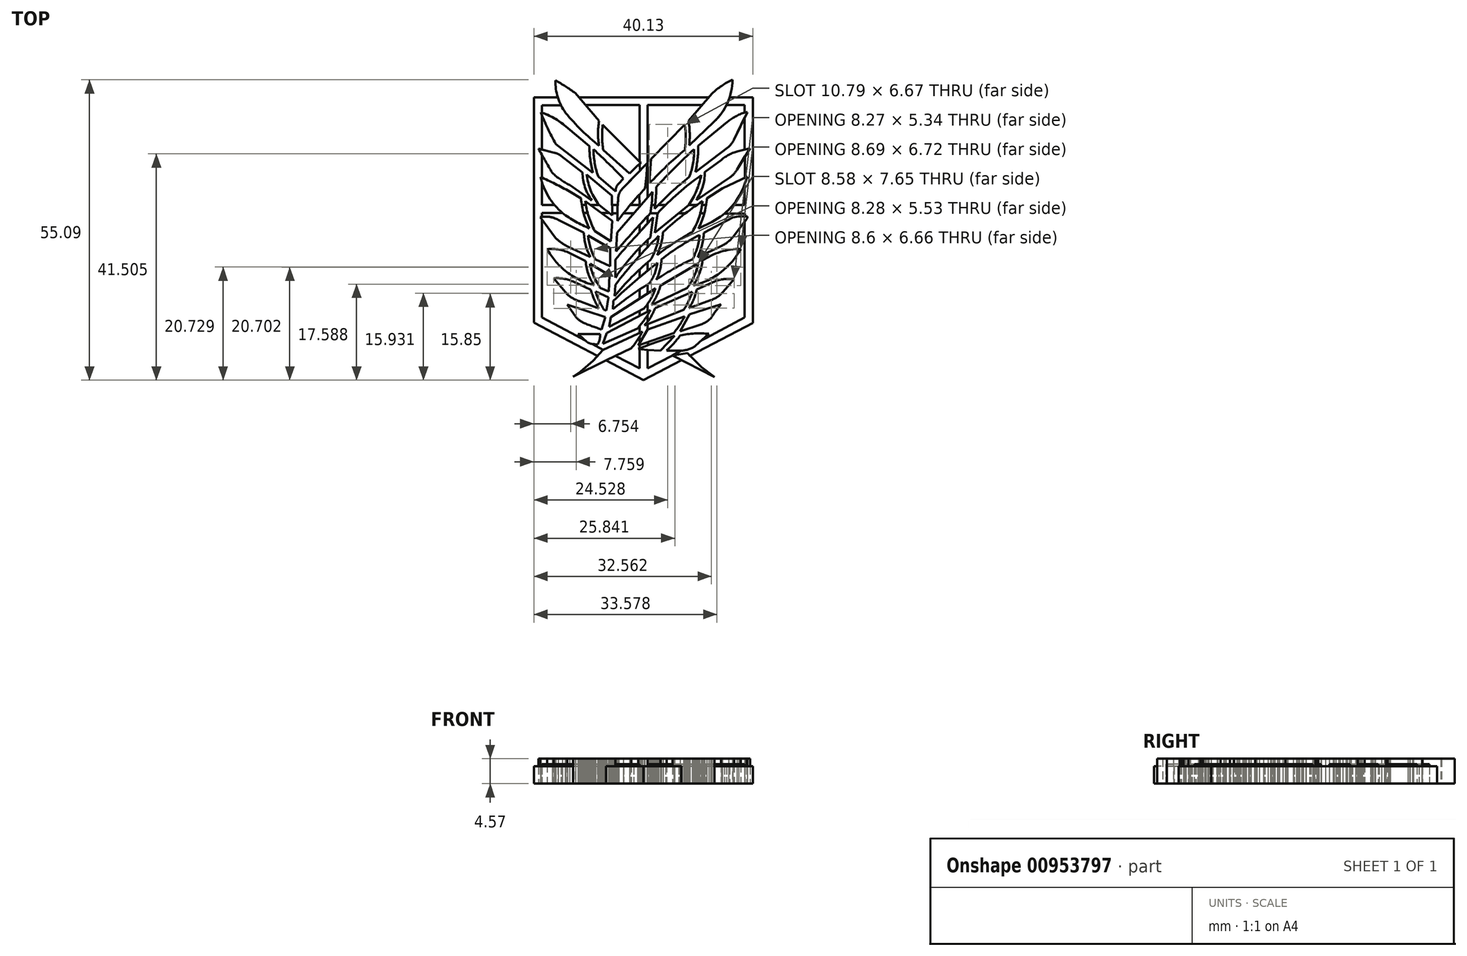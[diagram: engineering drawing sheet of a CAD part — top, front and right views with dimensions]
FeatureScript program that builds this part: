
annotation { "Feature Type Name" : "Feature", "Feature Type Description" : "" }
export const myFeature = defineFeature(function(context is Context, id is Id, definition is map)
    precondition{}
    {
        {
            var Q0;
            Q0=qCreatedBy(makeId("Top.planeOp"),FACE);
            var sketch = newSketch(context, id + "F0", { "sketchPlane" : qUnion([Q0])});
            skLineSegment(sketch, "E0", {"start": v(16.1, 29.15) * mm, "end": v(20.24, 29.15) * mm});
            skLineSegment(sketch, "E1", {"start": v(12.17, 29.15) * mm, "end": v(0, 29.15) * mm});
            skLineSegment(sketch, "E2", {"start": v(0, 29.15) * mm, "end": v(-11.4, 29.15) * mm});
            skLineSegment(sketch, "E3", {"start": v(-15.52, 29.15) * mm, "end": v(-19.9, 29.15) * mm});
            skLineSegment(sketch, "E4", {"start": v(-19.9, 29.15) * mm, "end": v(-19.9, 11.09) * mm});
            skLineSegment(sketch, "E5", {"start": v(-19.9, 11.09) * mm, "end": v(-19.9, -12.23) * mm});
            skLineSegment(sketch, "E6", {"start": v(20.24, 29.15) * mm, "end": v(20.24, -12.05) * mm});
            skLineSegment(sketch, "E7", {"start": v(20.24, -12.05) * mm, "end": v(20.24, -12.29) * mm});
            skLineSegment(sketch, "E8", {"start": v(20.24, -12.29) * mm, "end": v(8.8, -18.24) * mm});
            skLineSegment(sketch, "E9", {"start": v(-19.9, -12.23) * mm, "end": v(-8.29, -18.3) * mm});
            skLineSegment(sketch, "E10", {"start": v(7.13, -19.12) * mm, "end": v(0.17, -22.74) * mm});
            skLineSegment(sketch, "E11", {"start": v(-6.69, -19.14) * mm, "end": v(0.17, -22.74) * mm});
            skLineSegment(sketch, "E12", {"start": v(13.24, -22.16) * mm, "end": v(5.55, -18.25) * mm});
            skLineSegment(sketch, "E13", {"start": v(5.55, -18.25) * mm, "end": v(8.26, -17.77) * mm});
            skLineSegment(sketch, "E14", {"start": v(5.55, -18.25) * mm, "end": v(7.07, -17.34) * mm});
            skLineSegment(sketch, "E15", {"start": v(7.07, -17.34) * mm, "end": v(4.43, -17.34) * mm});
            skLineSegment(sketch, "E16", {"start": v(5.55, -18.25) * mm, "end": v(0.97, -20.6) * mm});
            skLineSegment(sketch, "E17", {"start": v(0.97, -20.6) * mm, "end": v(0.97, -17.2) * mm});
            skLineSegment(sketch, "E18", {"start": v(0.97, -17.2) * mm, "end": v(3.32, -17.33) * mm});
            skLineSegment(sketch, "E19", {"start": v(3.32, -17.33) * mm, "end": v(5.93, -14.63) * mm});
            skLineSegment(sketch, "E20", {"start": v(5.93, -14.63) * mm, "end": v(1.54, -16.12) * mm});
            skLineSegment(sketch, "E21", {"start": v(1.54, -16.12) * mm, "end": v(-0.76, -17.04) * mm});
            skLineSegment(sketch, "E22", {"start": v(-0.76, -17.04) * mm, "end": v(0.97, -17.2) * mm});
            skLineSegment(sketch, "E23", {"start": v(-0.48, -17.06) * mm, "end": v(-0.48, -20.6) * mm});
            skLineSegment(sketch, "E24", {"start": v(-0.48, -20.6) * mm, "end": v(-4.91, -18.28) * mm});
            skLineSegment(sketch, "E25", {"start": v(-4.91, -18.28) * mm, "end": v(-6.69, -19.14) * mm});
            skLineSegment(sketch, "E26", {"start": v(-4.91, -18.28) * mm, "end": v(-2.04, -16.91) * mm});
            skLineSegment(sketch, "E27", {"start": v(0, -13.88) * mm, "end": v(-7.25, -17.24) * mm});
            skLineSegment(sketch, "E28", {"start": v(-7.25, -17.24) * mm, "end": v(-9.03, -19.2) * mm});
            skLineSegment(sketch, "E29", {"start": v(-9.03, -19.2) * mm, "end": v(-11.34, -21.2) * mm});
            skLineSegment(sketch, "E30", {"start": v(-11.34, -21.2) * mm, "end": v(-12.67, -22.11) * mm});
            skLineSegment(sketch, "E31", {"start": v(-12.67, -22.11) * mm, "end": v(-6.69, -19.14) * mm});
            skLineSegment(sketch, "E32", {"start": v(13.24, -22.16) * mm, "end": v(10.87, -20.4) * mm});
            skLineSegment(sketch, "E33", {"start": v(10.87, -20.4) * mm, "end": v(8.44, -18) * mm});
            skLineSegment(sketch, "E34", {"start": v(8.44, -18) * mm, "end": v(8.26, -17.77) * mm});
            skLineSegment(sketch, "E35", {"start": v(-7.17, -17.2) * mm, "end": v(-8.96, -16.2) * mm});
            skLineSegment(sketch, "E36", {"start": v(-10.8, -15.26) * mm, "end": v(-13.03, -14.1) * mm});
            skLineSegment(sketch, "E37", {"start": v(-13.03, -14.1) * mm, "end": v(-18.38, -11.28) * mm});
            skLineSegment(sketch, "E38", {"start": v(-18.38, -11.28) * mm, "end": v(-18.38, 6.55) * mm});
            skLineSegment(sketch, "E39", {"start": v(-18.4, 7.29) * mm, "end": v(-18.4, 7.9) * mm});
            skLineSegment(sketch, "E40", {"start": v(-18.4, 7.9) * mm, "end": v(-14.63, 7.9) * mm});
            skLineSegment(sketch, "E41", {"start": v(-16.17, 9.39) * mm, "end": v(-18.43, 9.39) * mm});
            skLineSegment(sketch, "E42", {"start": v(-18.43, 9.39) * mm, "end": v(-18.43, 13.72) * mm});
            skLineSegment(sketch, "E43", {"start": v(-18.37, 14.54) * mm, "end": v(-18.37, 18.37) * mm});
            skLineSegment(sketch, "E44", {"start": v(-18.38, 19.6) * mm, "end": v(-18.38, 25.6) * mm});
            skLineSegment(sketch, "E45", {"start": v(-18.38, 26.45) * mm, "end": v(-18.38, 27.7) * mm});
            skLineSegment(sketch, "E46", {"start": v(-18.38, 27.7) * mm, "end": v(-14.9, 27.7) * mm});
            skLineSegment(sketch, "E47", {"start": v(-0.47, 27.72) * mm, "end": v(-0.47, 17.34) * mm});
            skLineSegment(sketch, "E48", {"start": v(0.87, 17) * mm, "end": v(-3.53, 12.52) * mm});
            skLineSegment(sketch, "E49", {"start": v(11.63, -15.06) * mm, "end": v(18.74, -11.27) * mm});
            skLineSegment(sketch, "E50", {"start": v(18.74, -11.27) * mm, "end": v(18.74, 6.23) * mm});
            skLineSegment(sketch, "E51", {"start": v(18.79, 7.3) * mm, "end": v(18.79, 7.82) * mm});
            skLineSegment(sketch, "E52", {"start": v(18.79, 7.82) * mm, "end": v(15.13, 7.82) * mm});
            skLineSegment(sketch, "E53", {"start": v(16.79, 9.36) * mm, "end": v(18.76, 9.36) * mm});
            skLineSegment(sketch, "E54", {"start": v(18.76, 9.36) * mm, "end": v(18.76, 13.2) * mm});
            skLineSegment(sketch, "E55", {"start": v(18.82, 14.36) * mm, "end": v(18.82, 18.12) * mm});
            skLineSegment(sketch, "E56", {"start": v(18.76, 19.6) * mm, "end": v(18.76, 25.26) * mm});
            skLineSegment(sketch, "E57", {"start": v(18.76, 26.36) * mm, "end": v(18.76, 27.7) * mm});
            skLineSegment(sketch, "E58", {"start": v(18.76, 27.7) * mm, "end": v(15.46, 27.7) * mm});
            skLineSegment(sketch, "E59", {"start": v(10.9, 27.7) * mm, "end": v(0.99, 27.7) * mm});
            skLineSegment(sketch, "E60", {"start": v(0.99, 27.7) * mm, "end": v(0.99, 10.9) * mm});
            skLineSegment(sketch, "E61", {"start": v(0.99, -5.3) * mm, "end": v(0.99, -6.88) * mm});
            skLineSegment(sketch, "E62", {"start": v(1.01, -16.33) * mm, "end": v(1.01, -15.8) * mm});
            skLineSegment(sketch, "E63", {"start": v(-11.05, 9.39) * mm, "end": v(-10.46, 9.39) * mm});
            skLineSegment(sketch, "E64", {"start": v(-9.34, 9.38) * mm, "end": v(-7.92, 9.38) * mm});
            skLineSegment(sketch, "E65", {"start": v(-5.5, 9.38) * mm, "end": v(-4.5, 9.38) * mm});
            skLineSegment(sketch, "E66", {"start": v(-9.98, 7.9) * mm, "end": v(-10.73, 7.9) * mm});
            skLineSegment(sketch, "E67", {"start": v(-7.34, 7.9) * mm, "end": v(-6.01, 7.9) * mm});
            skLineSegment(sketch, "E68", {"start": v(-5.48, 7.87) * mm, "end": v(-4.52, 7.87) * mm});
            skLineSegment(sketch, "E69", {"start": v(-3.37, 7.87) * mm, "end": v(-1.68, 7.87) * mm});
            skLineSegment(sketch, "E70", {"start": v(-2.16, 9.36) * mm, "end": v(-0.5, 9.36) * mm});
            skLineSegment(sketch, "E71", {"start": v(1.46, 7.87) * mm, "end": v(2.78, 7.87) * mm});
            skPoint(sketch, "E72.startSnap0", {"position": v(2.07, 9.36) * mm});
            skPoint(sketch, "E72.endSnap0", {"position": v(2.07, 9.36) * mm});
            skLineSegment(sketch, "E73", {"start": v(8.53, 9.36) * mm, "end": v(9.97, 9.36) * mm});
            skLineSegment(sketch, "E74", {"start": v(11.36, 7.87) * mm, "end": v(10.64, 7.87) * mm});
            skLineSegment(sketch, "E75", {"start": v(7.88, 7.87) * mm, "end": v(6.49, 7.87) * mm});
            skLineSegment(sketch, "E76", {"start": v(-0.5, -6.33) * mm, "end": v(-0.5, -7.7) * mm});
            skLineSegment(sketch, "E77", {"start": v(-0.5, -10.05) * mm, "end": v(-0.5, -10.94) * mm});
            skLineSegment(sketch, "E78", {"start": v(-0.86, -13.26) * mm, "end": v(-7.22, -16.08) * mm});
            skLineSegment(sketch, "E79", {"start": v(-7.22, -16.08) * mm, "end": v(-6.55, -14.1) * mm});
            skLineSegment(sketch, "E80", {"start": v(-6.55, -14.1) * mm, "end": v(1.48, -9.93) * mm});
            skLineSegment(sketch, "E81", {"start": v(-6.1, -12.95) * mm, "end": v(0.3, -9.61) * mm});
            skLineSegment(sketch, "E82", {"start": v(-6.1, -12.95) * mm, "end": v(-5.74, -11.18) * mm});
            skLineSegment(sketch, "E83", {"start": v(-5.74, -11.18) * mm, "end": v(2.42, -5.92) * mm});
            skArc(sketch, "E84", {"start": v(0.3, -9.61) * mm, "mid": v(1.54, -7.87) * mm, "end": v(2.42, -5.92) * mm});
            skArc(sketch, "E85", {"start": v(-2.04, -16.91) * mm, "mid": v(-0.94, -15.45) * mm, "end": v(0, -13.88) * mm});
            skArc(sketch, "E86", {"start": v(-0.86, -13.26) * mm, "mid": v(0.4, -11.66) * mm, "end": v(1.48, -9.93) * mm});
            skArc(sketch, "E87", {"start": v(1.3, -4.97) * mm, "mid": v(2.27, -3.19) * mm, "end": v(2.77, -1.22) * mm});
            skArc(sketch, "E88", {"start": v(1.48, -0.72) * mm, "mid": v(2.47, 1.42) * mm, "end": v(3, 3.72) * mm});
            skArc(sketch, "E89", {"start": v(1.46, 7.87) * mm, "mid": v(1.74, 9.84) * mm, "end": v(1.83, 11.82) * mm});
            skArc(sketch, "E90", {"start": v(0.47, 12.39) * mm, "mid": v(0.76, 14.68) * mm, "end": v(0.87, 17) * mm});
            skArc(sketch, "E91", {"start": v(-3.53, 12.52) * mm, "mid": v(-3.98, 11.97) * mm, "end": v(-4.33, 11.34) * mm});
            skArc(sketch, "E92", {"start": v(1.46, 7.87) * mm, "mid": v(-1.71, 4.41) * mm, "end": v(-4.8, 0.9) * mm});
            skLineSegment(sketch, "E93", {"start": v(-4.8, 0.9) * mm, "end": v(-4.62, 4.28) * mm});
            skLineSegment(sketch, "E94", {"start": v(-4.62, 4.28) * mm, "end": v(1.83, 11.82) * mm});
            skLineSegment(sketch, "E95", {"start": v(2, 7.1) * mm, "end": v(1.49, 3.44) * mm});
            skArc(sketch, "E96", {"start": v(1.49, 3.44) * mm, "mid": v(-1.95, -0.06) * mm, "end": v(-4.95, -3.93) * mm});
            skLineSegment(sketch, "E97", {"start": v(-4.95, -3.93) * mm, "end": v(-4.95, -0.62) * mm});
            skArc(sketch, "E98", {"start": v(2, 7.1) * mm, "mid": v(-1.52, 3.28) * mm, "end": v(-4.95, -0.62) * mm});
            skArc(sketch, "E99", {"start": v(3, 3.72) * mm, "mid": v(-1.14, -0.63) * mm, "end": v(-4.95, -5.28) * mm});
            skLineSegment(sketch, "E100", {"start": v(-5.06, -7.3) * mm, "end": v(-4.95, -5.28) * mm});
            skArc(sketch, "E101", {"start": v(1.48, -0.72) * mm, "mid": v(-1.95, -3.85) * mm, "end": v(-5.06, -7.3) * mm});
            skArc(sketch, "E102", {"start": v(1.3, -4.97) * mm, "mid": v(-2.13, -7.23) * mm, "end": v(-5.4, -9.71) * mm});
            skArc(sketch, "E103", {"start": v(2.77, -1.22) * mm, "mid": v(-1.35, -4.62) * mm, "end": v(-5.32, -8.2) * mm});
            skLineSegment(sketch, "E104", {"start": v(-5.32, -8.2) * mm, "end": v(-5.4, -9.71) * mm});
            skArc(sketch, "E105", {"start": v(-8.59, -6.46) * mm, "mid": v(-7.92, -8.2) * mm, "end": v(-7.02, -9.82) * mm});
            skArc(sketch, "E106", {"start": v(-9.43, -6.19) * mm, "mid": v(-8.83, -7.93) * mm, "end": v(-7.99, -9.57) * mm});
            skArc(sketch, "E107", {"start": v(-10.38, -0.93) * mm, "mid": v(-9.91, -3.24) * mm, "end": v(-8.84, -5.34) * mm});
            skArc(sketch, "E108", {"start": v(-9.6, -1.4) * mm, "mid": v(-8.89, -3.73) * mm, "end": v(-7.66, -5.84) * mm});
            skArc(sketch, "E109", {"start": v(-9.96, 3.78) * mm, "mid": v(-9.49, 1.52) * mm, "end": v(-8.61, -0.6) * mm});
            skArc(sketch, "E110", {"start": v(-10.7, 4.27) * mm, "mid": v(-10.4, 2.08) * mm, "end": v(-9.6, 0) * mm});
            skArc(sketch, "E111", {"start": v(-10.48, 10.08) * mm, "mid": v(-9.83, 7.27) * mm, "end": v(-8.74, 4.6) * mm});
            skArc(sketch, "E112", {"start": v(-11.23, 10.58) * mm, "mid": v(-10.75, 7.75) * mm, "end": v(-9.7, 5.09) * mm});
            skArc(sketch, "E113", {"start": v(-10.98, 15.35) * mm, "mid": v(-10.5, 12.65) * mm, "end": v(-9.25, 10.21) * mm});
            skArc(sketch, "E114", {"start": v(-10.18, 14.96) * mm, "mid": v(-9.45, 12) * mm, "end": v(-7.92, 9.38) * mm});
            skArc(sketch, "E115", {"start": v(-8.95, 19.58) * mm, "mid": v(-8.73, 17.05) * mm, "end": v(-8.08, 14.6) * mm});
            skArc(sketch, "E116", {"start": v(-9.73, 20.21) * mm, "mid": v(-9.53, 17.73) * mm, "end": v(-9.04, 15.28) * mm});
            skArc(sketch, "E117", {"start": v(-7.26, 24.1) * mm, "mid": v(-7.37, 21.78) * mm, "end": v(-7.16, 19.49) * mm});
            skArc(sketch, "E118", {"start": v(-7.92, 24.8) * mm, "mid": v(-8.13, 22.52) * mm, "end": v(-7.92, 20.23) * mm});
            skLineSegment(sketch, "E119", {"start": v(-7.26, 24.1) * mm, "end": v(-0.47, 17.34) * mm});
            skLineSegment(sketch, "E120", {"start": v(-0.47, 17.34) * mm, "end": v(-0.22, 17.14) * mm});
            skLineSegment(sketch, "E121", {"start": v(-2.33, 15.15) * mm, "end": v(-7.16, 19.49) * mm});
            skLineSegment(sketch, "E122", {"start": v(-0.47, -16.38) * mm, "end": v(-0.47, -16.92) * mm});
            skArc(sketch, "E123", {"start": v(0.47, 12.39) * mm, "mid": v(-2.12, 9.49) * mm, "end": v(-4.54, 6.44) * mm});
            skArc(sketch, "E124", {"start": v(-4.33, 11.34) * mm, "mid": v(-4.54, 8.9) * mm, "end": v(-4.54, 6.44) * mm});
            skArc(sketch, "E125", {"start": v(-0.22, 17.14) * mm, "mid": v(-1.33, 16.2) * mm, "end": v(-2.33, 15.15) * mm});
            skLineSegment(sketch, "E126", {"start": v(-12.28, 29.93) * mm, "end": v(-7.92, 24.8) * mm});
            skArc(sketch, "E127", {"start": v(-12.28, 29.93) * mm, "mid": v(-14.08, 31.14) * mm, "end": v(-15.94, 32.25) * mm});
            skArc(sketch, "E128", {"start": v(-15.94, 32.25) * mm, "mid": v(-15.5, 29.12) * mm, "end": v(-14.07, 26.3) * mm});
            skArc(sketch, "E129", {"start": v(-14.07, 26.3) * mm, "mid": v(-11.14, 23.11) * mm, "end": v(-7.92, 20.23) * mm});
            skArc(sketch, "E130", {"start": v(-14.04, 23.8) * mm, "mid": v(-16.2, 25.34) * mm, "end": v(-18.62, 26.4) * mm});
            skArc(sketch, "E131", {"start": v(-18.62, 26.4) * mm, "mid": v(-17.35, 23.44) * mm, "end": v(-15.89, 20.56) * mm});
            skLineSegment(sketch, "E132", {"start": v(-15.89, 20.56) * mm, "end": v(-9.04, 15.28) * mm});
            skLineSegment(sketch, "E133", {"start": v(-14.04, 23.8) * mm, "end": v(-9.73, 20.21) * mm});
            skLineSegment(sketch, "E134", {"start": v(-10.18, 14.96) * mm, "end": v(-5.58, 11.12) * mm});
            skLineSegment(sketch, "E135", {"start": v(-5.58, 11.12) * mm, "end": v(-5.48, 7.46) * mm});
            skLineSegment(sketch, "E136", {"start": v(-5.48, 7.46) * mm, "end": v(-7.92, 9.38) * mm});
            skLineSegment(sketch, "E137", {"start": v(-5.48, 6.49) * mm, "end": v(-10.48, 10.08) * mm});
            skLineSegment(sketch, "E138", {"start": v(-5.48, 6.49) * mm, "end": v(-5.77, 2.74) * mm});
            skLineSegment(sketch, "E139", {"start": v(-5.77, 2.74) * mm, "end": v(-8.74, 4.6) * mm});
            skArc(sketch, "E140", {"start": v(-3.46, 14.22) * mm, "mid": v(-6.16, 16.95) * mm, "end": v(-8.95, 19.58) * mm});
            skArc(sketch, "E141", {"start": v(-4.34, 13.27) * mm, "mid": v(-4.78, 12.63) * mm, "end": v(-4.9, 11.85) * mm});
            skLineSegment(sketch, "E142", {"start": v(-4.34, 13.27) * mm, "end": v(-3.46, 14.22) * mm});
            skLineSegment(sketch, "E143", {"start": v(-4.9, 11.85) * mm, "end": v(-8.08, 14.6) * mm});
            skLineSegment(sketch, "E144", {"start": v(-9.96, 3.78) * mm, "end": v(-5.86, 1.48) * mm});
            skLineSegment(sketch, "E145", {"start": v(-5.92, -1.88) * mm, "end": v(-5.86, 1.48) * mm});
            skLineSegment(sketch, "E146", {"start": v(-5.92, -1.88) * mm, "end": v(-8.61, -0.6) * mm});
            skLineSegment(sketch, "E147", {"start": v(-7.66, -5.84) * mm, "end": v(-6.13, -6.5) * mm});
            skLineSegment(sketch, "E148", {"start": v(-9.6, -1.4) * mm, "end": v(-6.04, -3.49) * mm});
            skLineSegment(sketch, "E149", {"start": v(-6.04, -3.49) * mm, "end": v(-6.13, -6.5) * mm});
            skLineSegment(sketch, "E150", {"start": v(-10.98, 15.35) * mm, "end": v(-14.9, 18.4) * mm});
            skArc(sketch, "E151", {"start": v(-14.9, 18.4) * mm, "mid": v(-15.5, 18.76) * mm, "end": v(-16.16, 18.97) * mm});
            skLineSegment(sketch, "E152", {"start": v(-16.16, 18.97) * mm, "end": v(-19.04, 19.74) * mm});
            skArc(sketch, "E153", {"start": v(-19.04, 19.74) * mm, "mid": v(-17.8, 17.5) * mm, "end": v(-16.52, 15.28) * mm});
            skLineSegment(sketch, "E154", {"start": v(-9.25, 10.21) * mm, "end": v(-13.32, 13.04) * mm});
            skArc(sketch, "E155", {"start": v(-16.52, 15.28) * mm, "mid": v(-14.99, 14.06) * mm, "end": v(-13.32, 13.04) * mm});
            skArc(sketch, "E156", {"start": v(-13.32, 11.86) * mm, "mid": v(-15.98, 13.25) * mm, "end": v(-18.68, 14.55) * mm});
            skLineSegment(sketch, "E157", {"start": v(-13.32, 11.86) * mm, "end": v(-11.23, 10.58) * mm});
            skLineSegment(sketch, "E158", {"start": v(-18.37, 14.54) * mm, "end": v(-18.37, 14.4) * mm});
            skArc(sketch, "E159", {"start": v(-18.68, 14.55) * mm, "mid": v(-17.18, 10.9) * mm, "end": v(-14.63, 7.9) * mm});
            skArc(sketch, "E160", {"start": v(-14.63, 7.9) * mm, "mid": v(-12.26, 6.34) * mm, "end": v(-9.7, 5.09) * mm});
            skArc(sketch, "E161", {"start": v(-15.45, 6.67) * mm, "mid": v(-17.03, 7.2) * mm, "end": v(-18.7, 7.16) * mm});
            skLineSegment(sketch, "E162", {"start": v(-18.7, 7.16) * mm, "end": v(-15.93, 3.36) * mm});
            skArc(sketch, "E163", {"start": v(-15.93, 3.36) * mm, "mid": v(-14.87, 2.48) * mm, "end": v(-13.7, 1.76) * mm});
            skLineSegment(sketch, "E164", {"start": v(-13.7, 1.76) * mm, "end": v(-9.6, -0.12) * mm});
            skLineSegment(sketch, "E165", {"start": v(-9.6, -0.12) * mm, "end": v(-9.6, 0) * mm});
            skLineSegment(sketch, "E166", {"start": v(-15.45, 6.67) * mm, "end": v(-10.7, 4.27) * mm});
            skArc(sketch, "E167", {"start": v(-14.15, -2.69) * mm, "mid": v(-11.62, -4.27) * mm, "end": v(-8.84, -5.34) * mm});
            skArc(sketch, "E168", {"start": v(-17.44, 1.28) * mm, "mid": v(-15.98, -0.86) * mm, "end": v(-14.15, -2.69) * mm});
            skArc(sketch, "E169", {"start": v(-13.08, 0.45) * mm, "mid": v(-15.2, 1.18) * mm, "end": v(-17.44, 1.28) * mm});
            skLineSegment(sketch, "E170", {"start": v(-13.08, 0.45) * mm, "end": v(-10.38, -0.93) * mm});
            skLineSegment(sketch, "E171", {"start": v(-9.43, -6.19) * mm, "end": v(-12.71, -4.67) * mm});
            skArc(sketch, "E172", {"start": v(-12.71, -4.67) * mm, "mid": v(-14.45, -4.13) * mm, "end": v(-16.27, -4.08) * mm});
            skLineSegment(sketch, "E173", {"start": v(-16.27, -4.08) * mm, "end": v(-13.7, -7.08) * mm});
            skArc(sketch, "E174", {"start": v(-13.7, -7.08) * mm, "mid": v(-12.64, -7.8) * mm, "end": v(-11.46, -8.3) * mm});
            skLineSegment(sketch, "E175", {"start": v(-11.46, -8.3) * mm, "end": v(-7.99, -9.57) * mm});
            skLineSegment(sketch, "E176", {"start": v(-13.76, -8.87) * mm, "end": v(-6.8, -11.18) * mm});
            skLineSegment(sketch, "E177", {"start": v(-6.8, -11.18) * mm, "end": v(-7.46, -13.48) * mm});
            skArc(sketch, "E178", {"start": v(-10.74, -12.25) * mm, "mid": v(-9.1, -12.89) * mm, "end": v(-7.46, -13.48) * mm});
            skArc(sketch, "E179", {"start": v(-12.26, -11.07) * mm, "mid": v(-11.57, -11.75) * mm, "end": v(-10.74, -12.25) * mm});
            skLineSegment(sketch, "E180", {"start": v(-13.76, -8.87) * mm, "end": v(-12.26, -11.07) * mm});
            skLineSegment(sketch, "E181", {"start": v(-11.8, -14.28) * mm, "end": v(-7.75, -14.28) * mm});
            skArc(sketch, "E182", {"start": v(-8.15, -16.2) * mm, "mid": v(-7.82, -15.27) * mm, "end": v(-7.75, -14.28) * mm});
            skLineSegment(sketch, "E183", {"start": v(-11.8, -14.28) * mm, "end": v(-11.56, -14.48) * mm});
            skLineSegment(sketch, "E184", {"start": v(-11.56, -14.48) * mm, "end": v(-10.23, -15.67) * mm});
            skArc(sketch, "E185", {"start": v(-10.23, -15.67) * mm, "mid": v(-9.8, -15.95) * mm, "end": v(-9.29, -16.1) * mm});
            skLineSegment(sketch, "E186", {"start": v(-9.29, -16.1) * mm, "end": v(-8.15, -16.2) * mm});
            skLineSegment(sketch, "E187", {"start": v(0.99, -13.47) * mm, "end": v(-0.75, -16.38) * mm});
            skLineSegment(sketch, "E188", {"start": v(-0.75, -16.38) * mm, "end": v(5.8, -14.08) * mm});
            skLineSegment(sketch, "E189", {"start": v(0.99, -13.47) * mm, "end": v(7.78, -11.07) * mm});
            skArc(sketch, "E190", {"start": v(5.8, -14.08) * mm, "mid": v(6.85, -12.62) * mm, "end": v(7.78, -11.07) * mm});
            skArc(sketch, "E191", {"start": v(7.57, -9.86) * mm, "mid": v(8.48, -8.25) * mm, "end": v(9.18, -6.54) * mm});
            skArc(sketch, "E192", {"start": v(0.38, -12.71) * mm, "mid": v(1.52, -11.23) * mm, "end": v(2.35, -9.56) * mm});
            skArc(sketch, "E193", {"start": v(1.66, -8.98) * mm, "mid": v(2.64, -7.28) * mm, "end": v(3.31, -5.44) * mm});
            skArc(sketch, "E194", {"start": v(2.62, -4.21) * mm, "mid": v(3.27, -2.44) * mm, "end": v(3.52, -0.57) * mm});
            skArc(sketch, "E195", {"start": v(2.73, 0.2) * mm, "mid": v(3.44, 2.29) * mm, "end": v(3.81, 4.45) * mm});
            skLineSegment(sketch, "E196", {"start": v(2.32, 4.3) * mm, "end": v(2.78, 7.87) * mm});
            skArc(sketch, "E197", {"start": v(7.07, -17.34) * mm, "mid": v(8.48, -17.11) * mm, "end": v(9.74, -16.45) * mm});
            skLineSegment(sketch, "E198", {"start": v(9.74, -16.45) * mm, "end": v(12.23, -14.26) * mm});
            skArc(sketch, "E199", {"start": v(12.23, -14.26) * mm, "mid": v(9.58, -14.2) * mm, "end": v(6.96, -14.53) * mm});
            skArc(sketch, "E200", {"start": v(4.43, -17.34) * mm, "mid": v(5.77, -16) * mm, "end": v(6.96, -14.53) * mm});
            skPoint(sketch, "E201.endSnap0", {"position": v(10.99, -15.36) * mm});
            skLineSegment(sketch, "E202", {"start": v(11.63, -15.06) * mm, "end": v(10.99, -15.36) * mm});
            skLineSegment(sketch, "E203", {"start": v(-11.4, 29.15) * mm, "end": v(-11.62, 29.15) * mm});
            skLineSegment(sketch, "E204", {"start": v(-15.52, 29.15) * mm, "end": v(-15.48, 29.15) * mm});
            skLineSegment(sketch, "E205", {"start": v(-18.38, 26.45) * mm, "end": v(-18.38, 26.33) * mm});
            skLineSegment(sketch, "E206", {"start": v(-18.38, 25.6) * mm, "end": v(-18.38, 25.92) * mm});
            skLineSegment(sketch, "E207", {"start": v(-18.38, 19.6) * mm, "end": v(-18.38, 19.56) * mm});
            skLineSegment(sketch, "E208", {"start": v(-18.37, 18.37) * mm, "end": v(-18.37, 18.56) * mm});
            skLineSegment(sketch, "E209", {"start": v(-16.17, 9.39) * mm, "end": v(-16.07, 9.39) * mm});
            skLineSegment(sketch, "E210", {"start": v(-18.38, 6.55) * mm, "end": v(-18.38, 6.75) * mm});
            skLineSegment(sketch, "E211", {"start": v(-18.4, 7.29) * mm, "end": v(-18.4, 7.19) * mm});
            skLineSegment(sketch, "E212", {"start": v(-10.8, -15.26) * mm, "end": v(-10.45, -15.45) * mm});
            skLineSegment(sketch, "E213", {"start": v(-8.96, -16.2) * mm, "end": v(-9.14, -16.11) * mm});
            skLineSegment(sketch, "E214", {"start": v(-8.29, -18.3) * mm, "end": v(-8.22, -18.33) * mm});
            skLineSegment(sketch, "E215", {"start": v(-0.47, -16.38) * mm, "end": v(-0.47, -16.27) * mm});
            skLineSegment(sketch, "E216", {"start": v(1.01, -15.8) * mm, "end": v(1.01, -15.75) * mm});
            skLineSegment(sketch, "E217", {"start": v(0.38, -12.71) * mm, "end": v(7.57, -9.86) * mm});
            skLineSegment(sketch, "E218", {"start": v(-0.5, -6.33) * mm, "end": v(-0.5, -6.12) * mm});
            skLineSegment(sketch, "E219", {"start": v(0.99, -5.3) * mm, "end": v(0.99, -5.1) * mm});
            skArc(sketch, "E220", {"start": v(8.6, 20.28) * mm, "mid": v(8.69, 22.55) * mm, "end": v(8.47, 24.82) * mm});
            skLineSegment(sketch, "E221", {"start": v(8.47, 24.82) * mm, "end": v(12.77, 29.84) * mm});
            skLineSegment(sketch, "E222", {"start": v(10.9, 27.7) * mm, "end": v(10.96, 27.7) * mm});
            skArc(sketch, "E223", {"start": v(16.54, 32.35) * mm, "mid": v(14.54, 31.26) * mm, "end": v(12.77, 29.84) * mm});
            skArc(sketch, "E224", {"start": v(13.1, 24.64) * mm, "mid": v(15.63, 28.13) * mm, "end": v(16.54, 32.35) * mm});
            skLineSegment(sketch, "E225", {"start": v(15.46, 27.7) * mm, "end": v(15.4, 27.7) * mm});
            skLineSegment(sketch, "E226", {"start": v(16.1, 29.15) * mm, "end": v(15.99, 29.15) * mm});
            skArc(sketch, "E227", {"start": v(19.23, 26.41) * mm, "mid": v(19, 26.42) * mm, "end": v(18.76, 26.36) * mm});
            skLineSegment(sketch, "E228", {"start": v(19.23, 26.41) * mm, "end": v(16.78, 21.32) * mm});
            skArc(sketch, "E229", {"start": v(15.8, 20.02) * mm, "mid": v(16.35, 20.63) * mm, "end": v(16.78, 21.32) * mm});
            skLineSegment(sketch, "E230", {"start": v(15.8, 20.02) * mm, "end": v(9.7, 15.42) * mm});
            skArc(sketch, "E231", {"start": v(9.7, 15.42) * mm, "mid": v(10.13, 17.82) * mm, "end": v(10.23, 20.26) * mm});
            skLineSegment(sketch, "E232", {"start": v(10.23, 20.26) * mm, "end": v(15.55, 24.6) * mm});
            skArc(sketch, "E233", {"start": v(18.76, 26.36) * mm, "mid": v(17.07, 25.63) * mm, "end": v(15.55, 24.6) * mm});
            skLineSegment(sketch, "E234", {"start": v(13.1, 24.64) * mm, "end": v(8.6, 20.28) * mm});
            skLineSegment(sketch, "E235", {"start": v(9.89, 10.24) * mm, "end": v(16.07, 14.46) * mm});
            skArc(sketch, "E236", {"start": v(9.89, 10.24) * mm, "mid": v(11.05, 12.7) * mm, "end": v(11.46, 15.4) * mm});
            skArc(sketch, "E237", {"start": v(16.07, 14.46) * mm, "mid": v(16.78, 15.08) * mm, "end": v(17.32, 15.86) * mm});
            skLineSegment(sketch, "E238", {"start": v(17.32, 15.86) * mm, "end": v(19.74, 19.81) * mm});
            skLineSegment(sketch, "E239", {"start": v(19.74, 19.81) * mm, "end": v(17.48, 19.22) * mm});
            skLineSegment(sketch, "E240", {"start": v(18.82, 18.12) * mm, "end": v(18.82, 18.36) * mm});
            skArc(sketch, "E241", {"start": v(17.48, 19.22) * mm, "mid": v(15.9, 18.62) * mm, "end": v(14.5, 17.67) * mm});
            skLineSegment(sketch, "E242", {"start": v(11.46, 15.4) * mm, "end": v(14.5, 17.67) * mm});
            skArc(sketch, "E243", {"start": v(12.79, 6.3) * mm, "mid": v(16.45, 9.17) * mm, "end": v(18.76, 13.2) * mm});
            skLineSegment(sketch, "E244", {"start": v(18.76, 13.2) * mm, "end": v(19.23, 14.56) * mm});
            skLineSegment(sketch, "E245", {"start": v(19.23, 14.56) * mm, "end": v(14.7, 12.41) * mm});
            skLineSegment(sketch, "E246", {"start": v(14.7, 12.41) * mm, "end": v(11.82, 10.6) * mm});
            skArc(sketch, "E247", {"start": v(10.27, 5.08) * mm, "mid": v(11.32, 7.76) * mm, "end": v(11.82, 10.6) * mm});
            skLineSegment(sketch, "E248", {"start": v(10.27, 5.08) * mm, "end": v(12.79, 6.3) * mm});
            skLineSegment(sketch, "E249", {"start": v(16.79, 9.36) * mm, "end": v(16.6, 9.36) * mm});
            skLineSegment(sketch, "E250", {"start": v(15.13, 7.82) * mm, "end": v(15.07, 7.82) * mm});
            skLineSegment(sketch, "E251", {"start": v(15.07, 7.82) * mm, "end": v(15.05, 7.82) * mm});
            skArc(sketch, "E252", {"start": v(11.05, 10.1) * mm, "mid": v(7.33, 7.42) * mm, "end": v(3.81, 4.45) * mm});
            skArc(sketch, "E253", {"start": v(9.19, 4.45) * mm, "mid": v(10.41, 7.19) * mm, "end": v(11.05, 10.1) * mm});
            skArc(sketch, "E254", {"start": v(9.19, 4.45) * mm, "mid": v(5.88, 2.45) * mm, "end": v(2.73, 0.2) * mm});
            skLineSegment(sketch, "E255", {"start": v(10.64, 7.87) * mm, "end": v(10.61, 7.87) * mm});
            skLineSegment(sketch, "E256", {"start": v(17.65, 7.3) * mm, "end": v(19.26, 7.3) * mm});
            skArc(sketch, "E257", {"start": v(19.1, 6.81) * mm, "mid": v(19.25, 7.03) * mm, "end": v(19.26, 7.3) * mm});
            skLineSegment(sketch, "E258", {"start": v(19.1, 6.81) * mm, "end": v(16.83, 3.77) * mm});
            skLineSegment(sketch, "E259", {"start": v(18.74, 6.23) * mm, "end": v(18.74, 6.35) * mm});
            skLineSegment(sketch, "E260", {"start": v(18.76, 25.26) * mm, "end": v(18.76, 25.47) * mm});
            skLineSegment(sketch, "E261", {"start": v(18.76, 19.6) * mm, "end": v(18.76, 19.54) * mm});
            skLineSegment(sketch, "E262", {"start": v(16.6, 9.36) * mm, "end": v(16.6, 9.36) * mm});
            skLineSegment(sketch, "E263", {"start": v(18.79, 7.3) * mm, "end": v(18.79, 7.29) * mm});
            skLineSegment(sketch, "E264", {"start": v(7.13, -19.12) * mm, "end": v(7.23, -19.06) * mm});
            skLineSegment(sketch, "E265", {"start": v(8.8, -18.24) * mm, "end": v(8.65, -18.32) * mm});
            skLineSegment(sketch, "E266", {"start": v(-1.68, 7.87) * mm, "end": v(-1.54, 7.87) * mm});
            skLineSegment(sketch, "E267", {"start": v(-3.37, 7.87) * mm, "end": v(-3.47, 7.87) * mm});
            skLineSegment(sketch, "E268", {"start": v(-5.48, 7.87) * mm, "end": v(-5.52, 7.87) * mm});
            skLineSegment(sketch, "E269", {"start": v(-7.34, 7.9) * mm, "end": v(-7.49, 7.9) * mm});
            skLineSegment(sketch, "E270", {"start": v(-9.34, 9.38) * mm, "end": v(-9.58, 9.38) * mm});
            skLineSegment(sketch, "E271", {"start": v(-5.5, 9.38) * mm, "end": v(-5.56, 9.38) * mm});
            skLineSegment(sketch, "E272", {"start": v(-0.5, -7.7) * mm, "end": v(-0.5, -7.82) * mm});
            skLineSegment(sketch, "E273", {"start": v(-0.5, -10.03) * mm, "end": v(-0.5, -10.05) * mm});
            skLineSegment(sketch, "E274", {"start": v(-0.5, -10.94) * mm, "end": v(-0.5, -10.97) * mm});
            skLineSegment(sketch, "E275", {"start": v(-10.73, 7.9) * mm, "end": v(-10.8, 7.9) * mm});
            skLineSegment(sketch, "E276", {"start": v(-7.02, -9.82) * mm, "end": v(-6.57, -10) * mm});
            skLineSegment(sketch, "E277", {"start": v(-6.57, -10) * mm, "end": v(-6.22, -7.56) * mm});
            skLineSegment(sketch, "E278", {"start": v(-6.22, -7.56) * mm, "end": v(-8.59, -6.46) * mm});
            skLineSegment(sketch, "E279", {"start": v(0.99, 10.9) * mm, "end": v(0.99, 10.8) * mm});
            skLineSegment(sketch, "E280", {"start": v(-2.16, 9.36) * mm, "end": v(-2.18, 9.36) * mm});
            skLineSegment(sketch, "E281", {"start": v(-10.46, 9.39) * mm, "end": v(-10.33, 9.39) * mm});
            skLineSegment(sketch, "E282", {"start": v(-11.05, 9.39) * mm, "end": v(-11.11, 9.39) * mm});
            skLineSegment(sketch, "E283", {"start": v(-18.37, 14.4) * mm, "end": v(-18.37, 14.39) * mm});
            skLineSegment(sketch, "E284", {"start": v(-18.38, 26.33) * mm, "end": v(-18.38, 26.32) * mm});
            skLineSegment(sketch, "E285", {"start": v(-2.18, 9.36) * mm, "end": v(-2.23, 9.36) * mm});
            skLineSegment(sketch, "E286", {"start": v(12.17, 29.15) * mm, "end": v(12.18, 29.15) * mm});
            skLineSegment(sketch, "E287", {"start": v(2.32, 4.3) * mm, "end": v(8.53, 9.36) * mm});
            skArc(sketch, "E288", {"start": v(8.53, 9.36) * mm, "mid": v(9.93, 12) * mm, "end": v(10.82, 14.85) * mm});
            skArc(sketch, "E289", {"start": v(10.82, 14.85) * mm, "mid": v(6.62, 11.57) * mm, "end": v(2.78, 7.87) * mm});
            skLineSegment(sketch, "E290", {"start": v(7.88, 7.87) * mm, "end": v(8.04, 7.87) * mm});
            skArc(sketch, "E291", {"start": v(10.51, 3.89) * mm, "mid": v(6.9, 1.83) * mm, "end": v(3.52, -0.57) * mm});
            skArc(sketch, "E292", {"start": v(9.2, -0.57) * mm, "mid": v(10.08, 1.59) * mm, "end": v(10.51, 3.89) * mm});
            skArc(sketch, "E293", {"start": v(9.2, -0.57) * mm, "mid": v(5.87, -2.25) * mm, "end": v(2.7, -4.21) * mm});
            skArc(sketch, "E294", {"start": v(14.54, 1.9) * mm, "mid": v(15.8, 2.7) * mm, "end": v(16.83, 3.77) * mm});
            skLineSegment(sketch, "E295", {"start": v(14.54, 1.9) * mm, "end": v(10.16, -0.18) * mm});
            skArc(sketch, "E296", {"start": v(10.16, -0.18) * mm, "mid": v(10.93, 2) * mm, "end": v(11.3, 4.28) * mm});
            skLineSegment(sketch, "E297", {"start": v(11.3, 4.28) * mm, "end": v(16.57, 7.1) * mm});
            skLineSegment(sketch, "E298", {"start": v(16.57, 7.1) * mm, "end": v(17.65, 7.3) * mm});
            skLineSegment(sketch, "E299", {"start": v(1.6, 17.8) * mm, "end": v(7.79, 24.16) * mm});
            skArc(sketch, "E300", {"start": v(7.79, 19.51) * mm, "mid": v(7.97, 21.84) * mm, "end": v(7.79, 24.16) * mm});
            skArc(sketch, "E301", {"start": v(7.79, 19.51) * mm, "mid": v(4.46, 16.53) * mm, "end": v(1.3, 13.37) * mm});
            skLineSegment(sketch, "E302", {"start": v(1.6, 17.8) * mm, "end": v(1.3, 13.37) * mm});
            skArc(sketch, "E303", {"start": v(2.23, 8.66) * mm, "mid": v(2.48, 10.65) * mm, "end": v(2.54, 12.66) * mm});
            skArc(sketch, "E304", {"start": v(8.62, 14.53) * mm, "mid": v(5.3, 11.72) * mm, "end": v(2.23, 8.66) * mm});
            skArc(sketch, "E305", {"start": v(8.62, 14.53) * mm, "mid": v(9.28, 17.03) * mm, "end": v(9.5, 19.62) * mm});
            skArc(sketch, "E306", {"start": v(9.5, 19.62) * mm, "mid": v(5.95, 16.2) * mm, "end": v(2.54, 12.66) * mm});
            skLineSegment(sketch, "E307", {"start": v(1.66, -8.98) * mm, "end": v(8.19, -5.87) * mm});
            skArc(sketch, "E308", {"start": v(8.19, -5.87) * mm, "mid": v(9.48, -3.72) * mm, "end": v(10.24, -1.33) * mm});
            skLineSegment(sketch, "E309", {"start": v(3.31, -5.44) * mm, "end": v(10.24, -1.33) * mm});
            skLineSegment(sketch, "E310", {"start": v(2.35, -9.56) * mm, "end": v(9.18, -6.54) * mm});
            skLineSegment(sketch, "E311", {"start": v(8.68, -10.68) * mm, "end": v(6.92, -13.78) * mm});
            skLineSegment(sketch, "E312", {"start": v(8.68, -10.68) * mm, "end": v(14.4, -8.83) * mm});
            skLineSegment(sketch, "E313", {"start": v(6.92, -13.78) * mm, "end": v(10.83, -12.5) * mm});
            skArc(sketch, "E314", {"start": v(10.83, -12.5) * mm, "mid": v(12.15, -11.75) * mm, "end": v(13.1, -10.57) * mm});
            skLineSegment(sketch, "E315", {"start": v(13.1, -10.57) * mm, "end": v(14.4, -8.83) * mm});
            skLineSegment(sketch, "E316", {"start": v(8.53, -9.56) * mm, "end": v(12.5, -8.1) * mm});
            skLineSegment(sketch, "E317", {"start": v(9.99, -6.12) * mm, "end": v(13.31, -4.64) * mm});
            skArc(sketch, "E318", {"start": v(15.3, -4.22) * mm, "mid": v(14.28, -4.32) * mm, "end": v(13.31, -4.64) * mm});
            skLineSegment(sketch, "E319", {"start": v(15.3, -4.22) * mm, "end": v(16.8, -4.22) * mm});
            skLineSegment(sketch, "E320", {"start": v(16.8, -4.22) * mm, "end": v(14.8, -6.57) * mm});
            skArc(sketch, "E321", {"start": v(12.5, -8.1) * mm, "mid": v(13.76, -7.5) * mm, "end": v(14.8, -6.57) * mm});
            skArc(sketch, "E322", {"start": v(8.53, -9.56) * mm, "mid": v(9.42, -7.9) * mm, "end": v(9.99, -6.12) * mm});
            skArc(sketch, "E323", {"start": v(9.34, -5.4) * mm, "mid": v(10.44, -3.23) * mm, "end": v(11.02, -0.87) * mm});
            skArc(sketch, "E324", {"start": v(18.03, 1.32) * mm, "mid": v(14.35, 0.78) * mm, "end": v(11.02, -0.87) * mm});
            skArc(sketch, "E325", {"start": v(9.34, -5.4) * mm, "mid": v(14.4, -2.95) * mm, "end": v(18.03, 1.32) * mm});
            skLineSegment(sketch, "E326", {"start": v(2.62, -4.21) * mm, "end": v(2.57, -4.32) * mm});
            skLineSegment(sketch, "E327", {"start": v(2.57, -4.32) * mm, "end": v(2.7, -4.21) * mm});
            skLineSegment(sketch, "E328", {"start": v(-0.47, 27.72) * mm, "end": v(-10.4, 27.72) * mm});
            skLineSegment(sketch, "E329", {"start": v(-0.47, 16.95) * mm, "end": v(-0.46, 15.65) * mm});
            skLineSegment(sketch, "E330", {"start": v(-0.5, 9.36) * mm, "end": v(-0.56, 11.28) * mm});
            skLineSegment(sketch, "E331", {"start": v(10.95, 9.36) * mm, "end": v(11.68, 9.36) * mm});
            skLineSegment(sketch, "E332", {"start": v(4.24, 9.36) * mm, "end": v(2.9, 9.36) * mm});
            skLineSegment(sketch, "E333", {"start": v(2.34, 9.36) * mm, "end": v(1.69, 9.36) * mm});
            skLineSegment(sketch, "E334", {"start": v(-0.5, 5.74) * mm, "end": v(-0.5, 4.4) * mm});
            skLineSegment(sketch, "E335", {"start": v(0.99, 7.36) * mm, "end": v(0.99, 6.02) * mm});
            skLineSegment(sketch, "E336", {"start": v(-0.5, 1.5) * mm, "end": v(-0.5, 0.07) * mm});
            skLineSegment(sketch, "E337", {"start": v(0.99, 2.98) * mm, "end": v(0.99, 1.68) * mm});
            skLineSegment(sketch, "E338", {"start": v(-0.5, -2.46) * mm, "end": v(-0.5, -3.9) * mm});
            skLineSegment(sketch, "E339", {"start": v(0.99, -2.65) * mm, "end": v(0.99, -1.14) * mm});
            skLineSegment(sketch, "E340", {"start": v(-0.5, -12.84) * mm, "end": v(-0.5, -14.12) * mm});
            skLineSegment(sketch, "E341", {"start": v(0.99, -12.47) * mm, "end": v(0.99, -13.47) * mm});
            skLineSegment(sketch, "E342", {"start": v(-0.5, -14.77) * mm, "end": v(-0.5, -15.97) * mm});
            skLineSegment(sketch, "E343", {"start": v(0.99, -10.2) * mm, "end": v(0.99, -8.73) * mm});
            skLineSegment(sketch, "E344", {"start": v(0.99, -10.76) * mm, "end": v(0.99, -12) * mm});
            skSolve(sketch);
        }
        {
            var Q0;
            {var subQ26=sQuery(id+"F0.wireOp",EDGE,"E1");Q0=makeQuery(id+"F0.imprint","IMPRINT",FACE,{"disambiguationData":[TD([[makeQuery(id+"F0.imprint","IMPRINT",EDGE,{"derivedFrom":subQ26}),1.0]])]});}
            var Q1;
            {var subQ15=sQuery(id+"F0.wireOp",EDGE,"E0");Q1=makeQuery(id+"F0.imprint","IMPRINT",FACE,{"disambiguationData":[TD([[makeQuery(id+"F0.imprint","IMPRINT",EDGE,{"derivedFrom":subQ15}),-1.0]])]});}
            var Q2;
            {var subQ5=sQuery(id+"F0.wireOp",EDGE,"E331");Q2=makeQuery(id+"F0.imprint","IMPRINT",FACE,{"disambiguationData":[TD([[makeQuery(id+"F0.imprint","IMPRINT",EDGE,{"derivedFrom":subQ5}),-1.0]])]});}
            var Q3;
            {var subQ3=sQuery(id+"F0.wireOp",EDGE,"E75");var subQ7=sQuery(id+"F0.wireOp",EDGE,"E290");var subQ9=makeQuery(id+"F0.imprint","INTERSECT",VERTEX,{"derivedFrom":[subQ3,subQ7]});Q3=makeQuery(id+"F0.imprint","IMPRINT",FACE,{"disambiguationData":[TD([[makeQuery(id+"F0.imprint","IMPRINT",EDGE,{"disambiguationData":[TD([[subQ9,-1.0]])],"derivedFrom":subQ3}),-1.0]])]});}
            var Q4;
            {var subQ4=sQuery(id+"F0.wireOp",EDGE,"E71");Q4=makeQuery(id+"F0.imprint","IMPRINT",FACE,{"disambiguationData":[TD([[makeQuery(id+"F0.imprint","IMPRINT",EDGE,{"derivedFrom":subQ4}),1.0]])]});}
            var Q5;
            {var subQ5=sQuery(id+"F0.wireOp",EDGE,"E271");var subQ9=sQuery(id+"F0.wireOp",EDGE,"E65");var subQ11=makeQuery(id+"F0.imprint","INTERSECT",VERTEX,{"derivedFrom":[subQ9,subQ5]});Q5=makeQuery(id+"F0.imprint","IMPRINT",FACE,{"disambiguationData":[TD([[makeQuery(id+"F0.imprint","IMPRINT",EDGE,{"disambiguationData":[TD([[subQ11,-1.0]])],"derivedFrom":subQ9}),-1.0]])]});}
            var Q6;
            {var subQ6=sQuery(id+"F0.wireOp",EDGE,"E64");Q6=makeQuery(id+"F0.imprint","IMPRINT",FACE,{"disambiguationData":[TD([[makeQuery(id+"F0.imprint","IMPRINT",EDGE,{"derivedFrom":subQ6}),-1.0]])]});}
            var Q7;
            {var subQ9=sQuery(id+"F0.wireOp",EDGE,"E63");Q7=makeQuery(id+"F0.imprint","IMPRINT",FACE,{"disambiguationData":[TD([[makeQuery(id+"F0.imprint","IMPRINT",EDGE,{"derivedFrom":subQ9}),-1.0]])]});}
            var Q8;
            {var subQ37=sQuery(id+"F0.wireOp",EDGE,"E3");Q8=makeQuery(id+"F0.imprint","IMPRINT",FACE,{"disambiguationData":[TD([[makeQuery(id+"F0.imprint","IMPRINT",EDGE,{"derivedFrom":subQ37}),1.0]])]});}
            var Q9;
            {var subQ4=sQuery(id+"F0.wireOp",EDGE,"E10");Q9=makeQuery(id+"F0.imprint","IMPRINT",FACE,{"disambiguationData":[TD([[makeQuery(id+"F0.imprint","IMPRINT",EDGE,{"derivedFrom":subQ4}),-1.0]])]});}
            var Q10;
            {var subQ5=sQuery(id+"F0.wireOp",EDGE,"E62");Q10=makeQuery(id+"F0.imprint","IMPRINT",FACE,{"disambiguationData":[TD([[makeQuery(id+"F0.imprint","IMPRINT",EDGE,{"derivedFrom":subQ5}),1.0]])]});}
            var Q11;
            {var subQ9=sQuery(id+"F0.wireOp",EDGE,"E76");Q11=makeQuery(id+"F0.imprint","IMPRINT",FACE,{"disambiguationData":[TD([[makeQuery(id+"F0.imprint","IMPRINT",EDGE,{"derivedFrom":subQ9}),1.0]])]});}
            var Q12;
            {var subQ0=sQuery(id+"F0.wireOp",EDGE,"E336");Q12=makeQuery(id+"F0.imprint","IMPRINT",FACE,{"disambiguationData":[TD([[makeQuery(id+"F0.imprint","IMPRINT",EDGE,{"derivedFrom":subQ0}),1.0]])]});}
            var Q13;
            {var subQ0=sQuery(id+"F0.wireOp",EDGE,"E334");Q13=makeQuery(id+"F0.imprint","IMPRINT",FACE,{"disambiguationData":[TD([[makeQuery(id+"F0.imprint","IMPRINT",EDGE,{"derivedFrom":subQ0}),1.0]])]});}
            var Q14;
            {var subQ0=sQuery(id+"F0.wireOp",EDGE,"E338");Q14=makeQuery(id+"F0.imprint","IMPRINT",FACE,{"disambiguationData":[TD([[makeQuery(id+"F0.imprint","IMPRINT",EDGE,{"derivedFrom":subQ0}),1.0]])]});}
            var Q15;
            {var subQ9=sQuery(id+"F0.wireOp",EDGE,"E77");Q15=makeQuery(id+"F0.imprint","IMPRINT",FACE,{"disambiguationData":[TD([[makeQuery(id+"F0.imprint","IMPRINT",EDGE,{"derivedFrom":subQ9}),1.0]])]});}
            var Q16;
            {var subQ0=sQuery(id+"F0.wireOp",EDGE,"E340");Q16=makeQuery(id+"F0.imprint","IMPRINT",FACE,{"disambiguationData":[TD([[makeQuery(id+"F0.imprint","IMPRINT",EDGE,{"derivedFrom":subQ0}),1.0]])]});}
            extrude(context, id + "F1", {"entities" : qUnion([Q0, Q1, Q2, Q3, Q4, Q5, Q6, Q7, Q8, Q9, Q10, Q11, Q12, Q13, Q14, Q15, Q16]), "depth" : 3.17 * mm, "offsetDistance" : 25.4 * mm});
        }
        {
            var Q0;
            {var subQ51=sQuery(id+"F0.wireOp",EDGE,"E43");Q0=makeQuery(id+"F0.imprint","IMPRINT",FACE,{"disambiguationData":[TD([[makeQuery(id+"F0.imprint","IMPRINT",EDGE,{"derivedFrom":subQ51}),-1.0]])]});}
            var Q1;
            {var subQ39=sQuery(id+"F0.wireOp",EDGE,"E56");Q1=makeQuery(id+"F0.imprint","IMPRINT",FACE,{"disambiguationData":[TD([[makeQuery(id+"F0.imprint","IMPRINT",EDGE,{"derivedFrom":subQ39}),1.0]])]});}
            var Q2;
            Q2=makeQuery(id+"F0.imprint","IMPRINT",FACE,{"disambiguationData":[TD([[makeQuery(id+"F0.imprint","IMPRINT",EDGE,{"derivedFrom":sQuery(id+"F0.wireOp",EDGE,"E14")}),1.0]])]});
            var Q3;
            {var subQ45=sQuery(id+"F0.wireOp",EDGE,"E35");Q3=makeQuery(id+"F0.imprint","IMPRINT",FACE,{"disambiguationData":[TD([[makeQuery(id+"F0.imprint","IMPRINT",EDGE,{"derivedFrom":subQ45}),-1.0]])]});}
            var Q4;
            {var subQ12=sQuery(id+"F0.wireOp",EDGE,"E23");Q4=makeQuery(id+"F0.imprint","IMPRINT",FACE,{"disambiguationData":[TD([[makeQuery(id+"F0.imprint","IMPRINT",EDGE,{"derivedFrom":subQ12}),-1.0]])]});}
            var Q5;
            Q5=makeQuery(id+"F0.imprint","IMPRINT",FACE,{"disambiguationData":[TD([[makeQuery(id+"F0.imprint","IMPRINT",EDGE,{"derivedFrom":sQuery(id+"F0.wireOp",EDGE,"E53")}),1.0]])]});
            var Q6;
            {var subQ0=sQuery(id+"F0.wireOp",EDGE,"E41");Q6=makeQuery(id+"F0.imprint","IMPRINT",FACE,{"disambiguationData":[TD([[makeQuery(id+"F0.imprint","IMPRINT",EDGE,{"derivedFrom":subQ0}),-1.0]])]});}
            var Q7;
            Q7=makeQuery(id+"F0.imprint","IMPRINT",FACE,{"disambiguationData":[TD([[makeQuery(id+"F0.imprint","IMPRINT",EDGE,{"derivedFrom":sQuery(id+"F0.wireOp",EDGE,"E70")}),1.0]])]});
            extrude(context, id + "F2", {"entities" : qUnion([Q0, Q1, Q2, Q3, Q4, Q5, Q6, Q7]), "depth" : 3.56 * mm, "offsetDistance" : 25.4 * mm});
        }
        {
            var Q0;
            {var subQ1=sQuery(id+"F0.wireOp",EDGE,"E118");Q0=makeQuery(id+"F0.imprint","IMPRINT",FACE,{"disambiguationData":[TD([[makeQuery(id+"F0.imprint","IMPRINT",EDGE,{"derivedFrom":subQ1}),-1.0]])]});}
            var Q1;
            Q1=makeQuery(id+"F0.imprint","IMPRINT",FACE,{"disambiguationData":[TD([[makeQuery(id+"F0.imprint","IMPRINT",EDGE,{"derivedFrom":sQuery(id+"F0.wireOp",EDGE,"E117")}),1.0]])]});
            var Q2;
            Q2=makeQuery(id+"F0.imprint","IMPRINT",FACE,{"disambiguationData":[TD([[makeQuery(id+"F0.imprint","IMPRINT",EDGE,{"derivedFrom":sQuery(id+"F0.wireOp",EDGE,"E115")}),1.0]])]});
            var Q3;
            Q3=makeQuery(id+"F0.imprint","IMPRINT",FACE,{"disambiguationData":[TD([[makeQuery(id+"F0.imprint","IMPRINT",EDGE,{"derivedFrom":sQuery(id+"F0.wireOp",EDGE,"E116")}),-1.0]])]});
            var Q4;
            Q4=makeQuery(id+"F0.imprint","IMPRINT",FACE,{"disambiguationData":[TD([[makeQuery(id+"F0.imprint","IMPRINT",EDGE,{"derivedFrom":sQuery(id+"F0.wireOp",EDGE,"E113")}),-1.0]])]});
            var Q5;
            {var subQ4=sQuery(id+"F0.wireOp",EDGE,"E114");Q5=makeQuery(id+"F0.imprint","IMPRINT",FACE,{"disambiguationData":[TD([[makeQuery(id+"F0.imprint","IMPRINT",EDGE,{"derivedFrom":subQ4}),1.0]])]});}
            var Q6;
            {var subQ7=sQuery(id+"F0.wireOp",EDGE,"E138");Q6=makeQuery(id+"F0.imprint","IMPRINT",FACE,{"disambiguationData":[TD([[makeQuery(id+"F0.imprint","IMPRINT",EDGE,{"derivedFrom":subQ7}),-1.0]])]});}
            var Q7;
            {var subQ4=sQuery(id+"F0.wireOp",EDGE,"E157");Q7=makeQuery(id+"F0.imprint","IMPRINT",FACE,{"disambiguationData":[TD([[makeQuery(id+"F0.imprint","IMPRINT",EDGE,{"derivedFrom":subQ4}),-1.0]])]});}
            var Q8;
            Q8=makeQuery(id+"F0.imprint","IMPRINT",FACE,{"disambiguationData":[TD([[makeQuery(id+"F0.imprint","IMPRINT",EDGE,{"derivedFrom":sQuery(id+"F0.wireOp",EDGE,"E110")}),-1.0]])]});
            var Q9;
            Q9=makeQuery(id+"F0.imprint","IMPRINT",FACE,{"disambiguationData":[TD([[makeQuery(id+"F0.imprint","IMPRINT",EDGE,{"derivedFrom":sQuery(id+"F0.wireOp",EDGE,"E109")}),1.0]])]});
            var Q10;
            Q10=makeQuery(id+"F0.imprint","IMPRINT",FACE,{"disambiguationData":[TD([[makeQuery(id+"F0.imprint","IMPRINT",EDGE,{"derivedFrom":sQuery(id+"F0.wireOp",EDGE,"E108")}),1.0]])]});
            var Q11;
            Q11=makeQuery(id+"F0.imprint","IMPRINT",FACE,{"disambiguationData":[TD([[makeQuery(id+"F0.imprint","IMPRINT",EDGE,{"derivedFrom":sQuery(id+"F0.wireOp",EDGE,"E107")}),-1.0]])]});
            var Q12;
            Q12=makeQuery(id+"F0.imprint","IMPRINT",FACE,{"disambiguationData":[TD([[makeQuery(id+"F0.imprint","IMPRINT",EDGE,{"derivedFrom":sQuery(id+"F0.wireOp",EDGE,"E106")}),-1.0]])]});
            var Q13;
            Q13=makeQuery(id+"F0.imprint","IMPRINT",FACE,{"disambiguationData":[TD([[makeQuery(id+"F0.imprint","IMPRINT",EDGE,{"derivedFrom":sQuery(id+"F0.wireOp",EDGE,"E105")}),1.0]])]});
            var Q14;
            Q14=makeQuery(id+"F0.imprint","IMPRINT",FACE,{"disambiguationData":[TD([[makeQuery(id+"F0.imprint","IMPRINT",EDGE,{"derivedFrom":sQuery(id+"F0.wireOp",EDGE,"E176")}),-1.0]])]});
            var Q15;
            Q15=makeQuery(id+"F0.imprint","IMPRINT",FACE,{"disambiguationData":[TD([[makeQuery(id+"F0.imprint","IMPRINT",EDGE,{"derivedFrom":sQuery(id+"F0.wireOp",EDGE,"E181")}),-1.0]])]});
            var Q16;
            Q16=makeQuery(id+"F0.imprint","IMPRINT",FACE,{"disambiguationData":[TD([[makeQuery(id+"F0.imprint","IMPRINT",EDGE,{"derivedFrom":sQuery(id+"F0.wireOp",EDGE,"E25")}),-1.0]])]});
            var Q17;
            {var subQ4=sQuery(id+"F0.wireOp",EDGE,"E78");Q17=makeQuery(id+"F0.imprint","IMPRINT",FACE,{"disambiguationData":[TD([[makeQuery(id+"F0.imprint","IMPRINT",EDGE,{"derivedFrom":subQ4}),-1.0]])]});}
            var Q18;
            {var subQ1=sQuery(id+"F0.wireOp",EDGE,"E82");Q18=makeQuery(id+"F0.imprint","IMPRINT",FACE,{"disambiguationData":[TD([[makeQuery(id+"F0.imprint","IMPRINT",EDGE,{"derivedFrom":subQ1}),-1.0]])]});}
            var Q19;
            {var subQ3=sQuery(id+"F0.wireOp",EDGE,"E87");Q19=makeQuery(id+"F0.imprint","IMPRINT",FACE,{"disambiguationData":[TD([[makeQuery(id+"F0.imprint","IMPRINT",EDGE,{"derivedFrom":subQ3}),1.0]])]});}
            var Q20;
            {var subQ3=sQuery(id+"F0.wireOp",EDGE,"E88");Q20=makeQuery(id+"F0.imprint","IMPRINT",FACE,{"disambiguationData":[TD([[makeQuery(id+"F0.imprint","IMPRINT",EDGE,{"derivedFrom":subQ3}),1.0]])]});}
            var Q21;
            {var subQ4=sQuery(id+"F0.wireOp",EDGE,"E95");Q21=makeQuery(id+"F0.imprint","IMPRINT",FACE,{"disambiguationData":[TD([[makeQuery(id+"F0.imprint","IMPRINT",EDGE,{"derivedFrom":subQ4}),-1.0]])]});}
            var Q22;
            {var subQ8=sQuery(id+"F0.wireOp",EDGE,"E93");Q22=makeQuery(id+"F0.imprint","IMPRINT",FACE,{"disambiguationData":[TD([[makeQuery(id+"F0.imprint","IMPRINT",EDGE,{"derivedFrom":subQ8}),-1.0]])]});}
            var Q23;
            {var subQ6=sQuery(id+"F0.wireOp",EDGE,"E90");Q23=makeQuery(id+"F0.imprint","IMPRINT",FACE,{"disambiguationData":[TD([[makeQuery(id+"F0.imprint","IMPRINT",EDGE,{"derivedFrom":subQ6}),1.0]])]});}
            var Q24;
            Q24=makeQuery(id+"F0.imprint","IMPRINT",FACE,{"disambiguationData":[TD([[makeQuery(id+"F0.imprint","IMPRINT",EDGE,{"derivedFrom":sQuery(id+"F0.wireOp",EDGE,"E299")}),-1.0]])]});
            var Q25;
            {var subQ4=sQuery(id+"F0.wireOp",EDGE,"E220");Q25=makeQuery(id+"F0.imprint","IMPRINT",FACE,{"disambiguationData":[TD([[makeQuery(id+"F0.imprint","IMPRINT",EDGE,{"derivedFrom":subQ4}),-1.0]])]});}
            var Q26;
            {var subQ3=sQuery(id+"F0.wireOp",EDGE,"E196");Q26=makeQuery(id+"F0.imprint","IMPRINT",FACE,{"disambiguationData":[TD([[makeQuery(id+"F0.imprint","IMPRINT",EDGE,{"derivedFrom":subQ3}),-1.0]])]});}
            var Q27;
            Q27=makeQuery(id+"F0.imprint","IMPRINT",FACE,{"disambiguationData":[TD([[makeQuery(id+"F0.imprint","IMPRINT",EDGE,{"derivedFrom":sQuery(id+"F0.wireOp",EDGE,"E235")}),1.0]])]});
            var Q28;
            {var subQ7=sQuery(id+"F0.wireOp",EDGE,"E244");Q28=makeQuery(id+"F0.imprint","IMPRINT",FACE,{"disambiguationData":[TD([[makeQuery(id+"F0.imprint","IMPRINT",EDGE,{"derivedFrom":subQ7}),1.0]])]});}
            var Q29;
            {var subQ1=sQuery(id+"F0.wireOp",EDGE,"E195");Q29=makeQuery(id+"F0.imprint","IMPRINT",FACE,{"disambiguationData":[TD([[makeQuery(id+"F0.imprint","IMPRINT",EDGE,{"derivedFrom":subQ1}),-1.0]])]});}
            var Q30;
            Q30=makeQuery(id+"F0.imprint","IMPRINT",FACE,{"disambiguationData":[TD([[makeQuery(id+"F0.imprint","IMPRINT",EDGE,{"derivedFrom":sQuery(id+"F0.wireOp",EDGE,"E194")}),-1.0]])]});
            var Q31;
            {var subQ1=sQuery(id+"F0.wireOp",EDGE,"E257");Q31=makeQuery(id+"F0.imprint","IMPRINT",FACE,{"disambiguationData":[TD([[makeQuery(id+"F0.imprint","IMPRINT",EDGE,{"derivedFrom":subQ1}),1.0]])]});}
            var Q32;
            Q32=makeQuery(id+"F0.imprint","IMPRINT",FACE,{"disambiguationData":[TD([[makeQuery(id+"F0.imprint","IMPRINT",EDGE,{"derivedFrom":sQuery(id+"F0.wireOp",EDGE,"E323")}),-1.0]])]});
            var Q33;
            Q33=makeQuery(id+"F0.imprint","IMPRINT",FACE,{"disambiguationData":[TD([[makeQuery(id+"F0.imprint","IMPRINT",EDGE,{"derivedFrom":sQuery(id+"F0.wireOp",EDGE,"E193")}),-1.0]])]});
            var Q34;
            {var subQ6=sQuery(id+"F0.wireOp",EDGE,"E191");Q34=makeQuery(id+"F0.imprint","IMPRINT",FACE,{"disambiguationData":[TD([[makeQuery(id+"F0.imprint","IMPRINT",EDGE,{"derivedFrom":subQ6}),1.0]])]});}
            var Q35;
            Q35=makeQuery(id+"F0.imprint","IMPRINT",FACE,{"disambiguationData":[TD([[makeQuery(id+"F0.imprint","IMPRINT",EDGE,{"derivedFrom":sQuery(id+"F0.wireOp",EDGE,"E316")}),1.0]])]});
            var Q36;
            Q36=makeQuery(id+"F0.imprint","IMPRINT",FACE,{"disambiguationData":[TD([[makeQuery(id+"F0.imprint","IMPRINT",EDGE,{"derivedFrom":sQuery(id+"F0.wireOp",EDGE,"E311")}),1.0]])]});
            var Q37;
            {var subQ6=sQuery(id+"F0.wireOp",EDGE,"E189");Q37=makeQuery(id+"F0.imprint","IMPRINT",FACE,{"disambiguationData":[TD([[makeQuery(id+"F0.imprint","IMPRINT",EDGE,{"derivedFrom":subQ6}),-1.0]])]});}
            var Q38;
            {var subQ3=sQuery(id+"F0.wireOp",EDGE,"E18");Q38=makeQuery(id+"F0.imprint","IMPRINT",FACE,{"disambiguationData":[TD([[makeQuery(id+"F0.imprint","IMPRINT",EDGE,{"derivedFrom":subQ3}),1.0]])]});}
            var Q39;
            Q39=makeQuery(id+"F0.imprint","IMPRINT",FACE,{"disambiguationData":[TD([[makeQuery(id+"F0.imprint","IMPRINT",EDGE,{"derivedFrom":sQuery(id+"F0.wireOp",EDGE,"E15")}),-1.0]])]});
            var Q40;
            {var subQ1=sQuery(id+"F0.wireOp",EDGE,"E13");Q40=makeQuery(id+"F0.imprint","IMPRINT",FACE,{"disambiguationData":[TD([[makeQuery(id+"F0.imprint","IMPRINT",EDGE,{"derivedFrom":subQ1}),-1.0]])]});}
            var Q41;
            {var subQ4=sQuery(id+"F0.wireOp",EDGE,"E305");Q41=makeQuery(id+"F0.imprint","IMPRINT",FACE,{"disambiguationData":[TD([[makeQuery(id+"F0.imprint","IMPRINT",EDGE,{"derivedFrom":subQ4}),1.0]])]});}
            var Q42;
            {var subQ3=sQuery(id+"F0.wireOp",EDGE,"E227");Q42=makeQuery(id+"F0.imprint","IMPRINT",FACE,{"disambiguationData":[TD([[makeQuery(id+"F0.imprint","IMPRINT",EDGE,{"derivedFrom":subQ3}),1.0]])]});}
            extrude(context, id + "F3", {"entities" : qUnion([Q0, Q1, Q2, Q3, Q4, Q5, Q6, Q7, Q8, Q9, Q10, Q11, Q12, Q13, Q14, Q15, Q16, Q17, Q18, Q19, Q20, Q21, Q22, Q23, Q24, Q25, Q26, Q27, Q28, Q29, Q30, Q31, Q32, Q33, Q34, Q35, Q36, Q37, Q38, Q39, Q40, Q41, Q42]), "depth" : 4.57 * mm, "offsetDistance" : 25.4 * mm});
        }
    });
